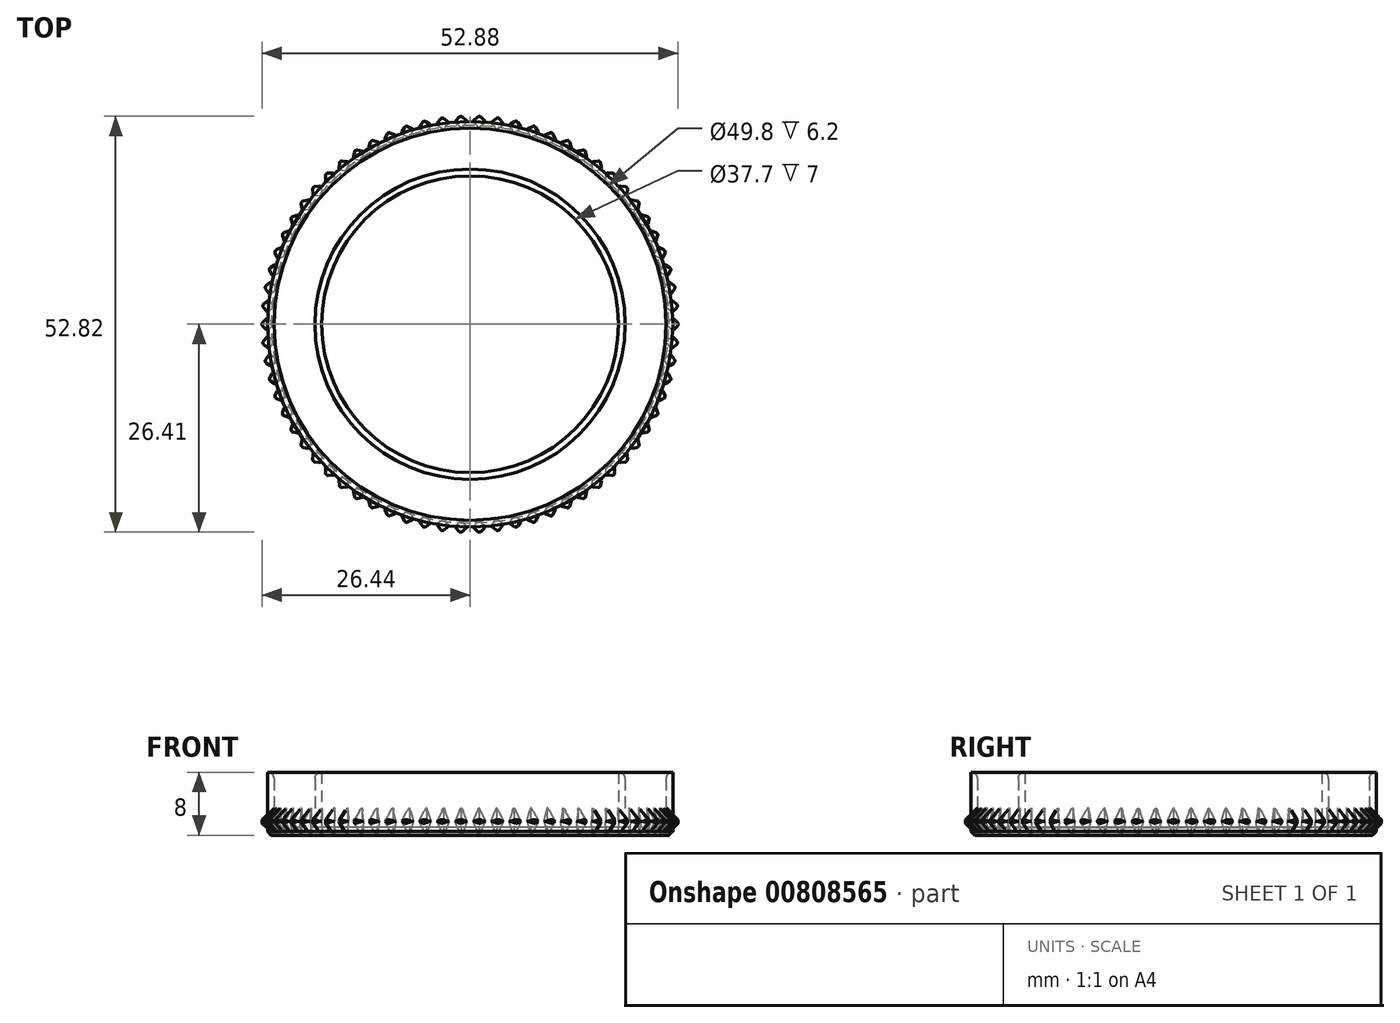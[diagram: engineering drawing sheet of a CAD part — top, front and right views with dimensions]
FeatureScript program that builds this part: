
annotation { "Feature Type Name" : "Feature", "Feature Type Description" : "" }
export const myFeature = defineFeature(function(context is Context, id is Id, definition is map)
    precondition{}
    {
        {
            var Q0;
            Q0=qCreatedBy(makeId("Top.planeOp"),FACE);
            var sketch = newSketch(context, id + "F0", { "sketchPlane" : qUnion([Q0])});
            skCircle(sketch, "E0", {"center": v(0, 0) * mm, "radius": 25.75 * mm});
            skSolve(sketch);
        }
        {
            var Q0;
            Q0=makeQuery(id+"F0.imprint","IMPRINT",FACE,{"disambiguationData":[TD([[makeQuery(id+"F0.imprint","IMPRINT",EDGE,{"derivedFrom":sQuery(id+"F0.wireOp",EDGE,"E0")}),1.0]])]});
            extrude(context, id + "F1", {"entities" : qUnion([Q0]), "depth" : 1 * mm, "offsetDistance" : 25 * mm});
        }
        {
            var Q0;
            Q0=makeQuery(id+"F1.opExtrude","CAP_FACE",FACE,{"disambiguationData":[OSD([sQuery(id+"F0.wireOp",EDGE,"E0")])],"isStart":false});
            var sketch = newSketch(context, id + "F2", { "sketchPlane" : qUnion([Q0])});
            skCircle(sketch, "E1", {"center": v(0, 0) * mm, "radius": 25.75 * mm});
            skCircle(sketch, "E2", {"center": v(0, 0) * mm, "radius": 24.9 * mm});
            skCircle(sketch, "E3", {"center": v(0, 0) * mm, "radius": 19.7 * mm});
            skCircle(sketch, "E4", {"center": v(0, 0) * mm, "radius": 18.85 * mm});
            skSolve(sketch);
        }
        {
            var Q0;
            Q0=makeQuery(id+"F2.imprint","IMPRINT",FACE,{"disambiguationData":[TD([[makeQuery(id+"F2.imprint","IMPRINT",EDGE,{"derivedFrom":sQuery(id+"F2.wireOp",EDGE,"E1")}),1.0]])]});
            var Q1;
            Q1=makeQuery(id+"F2.imprint","IMPRINT",FACE,{"disambiguationData":[TD([[makeQuery(id+"F2.imprint","IMPRINT",EDGE,{"derivedFrom":sQuery(id+"F2.wireOp",EDGE,"E3")}),1.0]])]});
            extrude(context, id + "F3", {"entities" : qUnion([Q0, Q1]), "operationType" : NewBodyOperationType.ADD, "depth" : 7 * mm, "offsetDistance" : 25 * mm});
        }
        {
            var Q0;
            Q0=makeQuery(id+"F3.opExtrude","CAP_EDGE",EDGE,{"disambiguationData":[OSD([sQuery(id+"F2.wireOp",EDGE,"E2")])],"isStart":false});
            var Q1;
            Q1=makeQuery(id+"F3.opExtrude","CAP_EDGE",EDGE,{"disambiguationData":[OSD([sQuery(id+"F2.wireOp",EDGE,"E3")])],"isStart":false});
            fillet(context, id + "F4", {"entities" : qUnion([Q0, Q1]), "radius" : 0.8 * mm, "tangentPropagation" : true, "allowEdgeOverflow" : false});
        }
        {
            var Q0;
            Q0=makeQuery(id+"F1.opExtrude","CAP_EDGE",EDGE,{"disambiguationData":[OSD([sQuery(id+"F0.wireOp",EDGE,"E0")])],"isStart":true});
            chamfer(context, id + "F5", {"entities" : qUnion([Q0]), "width" : 0.5 * mm, "tangentPropagation" : true});
        }
        {
            var Q0;
            Q0=qCreatedBy(makeId("Front.planeOp"),FACE);
            var sketch = newSketch(context, id + "F6", { "sketchPlane" : qUnion([Q0])});
            skLineSegment(sketch, "E5", {"start": v(-24.94, 3.63) * mm, "end": v(-26.56, 2.01) * mm});
            skLineSegment(sketch, "E6", {"start": v(-26.56, 2.01) * mm, "end": v(-26.56, 1.47) * mm});
            skLineSegment(sketch, "E7", {"start": v(-26.56, 1.47) * mm, "end": v(-24.94, -0.14) * mm});
            skLineSegment(sketch, "E8", {"start": v(-24.94, -0.14) * mm, "end": v(-24.94, 3.63) * mm});
            skSolve(sketch);
        }
        {
            var Q0;
            Q0 = qSketchRegion(id + "F6", true);
            extrude(context, id + "F7", {"entities" : qUnion([Q0]), "endBound" : BoundingType.SYMMETRIC, "depth" : 2 * mm, "offsetDistance" : 25 * mm, "hasDraft" : true, "draftAngle" : 45 * degree, "draftPullDirection" : true});
        }
        {
            var Q0;
            {var subQ0=makeQuery(id+"F7.opExtrude","SWEPT_FACE",FACE,{"disambiguationData":[OSD([sQuery(id+"F6.wireOp",EDGE,"E6")])]});Q0=makeQuery(id+"F7.*.booleanUnion.opBoolean","MERGE",EDGE,{"derivedFrom":[makeQuery(id+"F7.*.split.splitOp","SPLIT_SURFACE_INTERSECT",EDGE,{"derivedFrom":[subQ0]}),makeQuery(id+"F7.*.split.splitOp","SPLIT_SURFACE_INTERSECT",EDGE,{"derivedFrom":[subQ0],"isFromBackBody":true})]});}
            var Q1;
            {var subQ0=makeQuery(id+"F7.opExtrude","SWEPT_FACE",FACE,{"disambiguationData":[OSD([sQuery(id+"F6.wireOp",EDGE,"E7")])]});Q1=makeQuery(id+"F7.*.booleanUnion.opBoolean","MERGE",EDGE,{"derivedFrom":[makeQuery(id+"F7.*.split.splitOp","SPLIT_SURFACE_INTERSECT",EDGE,{"derivedFrom":[subQ0]}),makeQuery(id+"F7.*.split.splitOp","SPLIT_SURFACE_INTERSECT",EDGE,{"derivedFrom":[subQ0],"isFromBackBody":true})]});}
            var Q2;
            {var subQ0=makeQuery(id+"F7.opExtrude","SWEPT_FACE",FACE,{"disambiguationData":[OSD([sQuery(id+"F6.wireOp",EDGE,"E5")])]});Q2=makeQuery(id+"F7.*.booleanUnion.opBoolean","MERGE",EDGE,{"derivedFrom":[makeQuery(id+"F7.*.split.splitOp","SPLIT_SURFACE_INTERSECT",EDGE,{"derivedFrom":[subQ0]}),makeQuery(id+"F7.*.split.splitOp","SPLIT_SURFACE_INTERSECT",EDGE,{"derivedFrom":[subQ0],"isFromBackBody":true})]});}
            fillet(context, id + "F8", {"entities" : qUnion([Q0, Q1, Q2]), "radius" : 0.3 * mm, "tangentPropagation" : true, "allowEdgeOverflow" : false});
        }
        {
            var Q0;
            Q0=makeQuery(id+"F7.*.split.splitOp","SPLIT",BODY,{"derivedFrom":makeQuery(id+"F7.opExtrude","SWEPT_BODY",BODY,{"disambiguationData":[OSD([sQuery(id+"F6.wireOp",EDGE,"E5"),sQuery(id+"F6.wireOp",EDGE,"E6"),sQuery(id+"F6.wireOp",EDGE,"E7"),sQuery(id+"F6.wireOp",EDGE,"E8")])]})});
            var Q1;
            {var subQ0=sQuery(id+"F0.wireOp",EDGE,"E0");Q1=makeQuery(id+"F5.opChamfer","BLEND_EDGE",EDGE,{"blendedFrom":[makeQuery(id+"F1.opExtrude","CAP_EDGE",EDGE,{"disambiguationData":[OSD([subQ0])],"isStart":true}),makeQuery(id+"F3.boolean.opBoolean","MERGE",FACE,{"derivedFrom":[makeQuery(id+"F1.opExtrude","SWEPT_FACE",FACE,{"disambiguationData":[OSD([subQ0])]}),makeQuery(id+"F3.opExtrude","SWEPT_FACE",FACE,{"disambiguationData":[OSD([sQuery(id+"F2.wireOp",EDGE,"E1")])]})]})],"blendedInto":[makeQuery(id+"F3.boolean.opBoolean","MERGE",FACE,{"derivedFrom":[makeQuery(id+"F1.opExtrude","SWEPT_FACE",FACE,{"disambiguationData":[OSD([subQ0])]}),makeQuery(id+"F3.opExtrude","SWEPT_FACE",FACE,{"disambiguationData":[OSD([sQuery(id+"F2.wireOp",EDGE,"E1")])]})]})]});}
            circularPattern(context, id + "F9", {"entities" : qUnion([Q0]), "axis" : qUnion([Q1]), "angle" : 360 * degree, "instanceCount" : 70, "equalSpace" : true});
        }
    });
